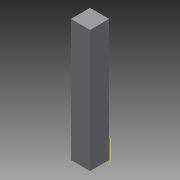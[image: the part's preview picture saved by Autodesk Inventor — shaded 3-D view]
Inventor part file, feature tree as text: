
AUTODESK INVENTOR PART (.ipt)
format: ipt  version: 2015 (Build 190159000, 159)  size: 68,096 bytes
history: native  units: in
note: dims shown in document units (in); Inventor stores cm internally (conversion verified against a paired STEP export)
features: reference x2, plane x1, extrude x1, sketch x1
ambient origin geometry x8: Origin, YZ Plane, XZ Plane, XY Plane, X Axis, Y Axis, Z Axis, Center Point
bodies: Solid1 (feature_tree)
feature tree (5):
  plane  "Work Plane1"
  extrude  "Extrusion1"  [1 undecoded]
  sketch  "Sketch1"  dims[d0=0.75in d1=0.0in]
  reference  "Reference1"
  reference  "Reference2"
note: 1 required parameter value undecoded (feature->parameter linkage not recoverable at this tier; creation-order binding heuristic only, values carry confidence <= 0.55)
